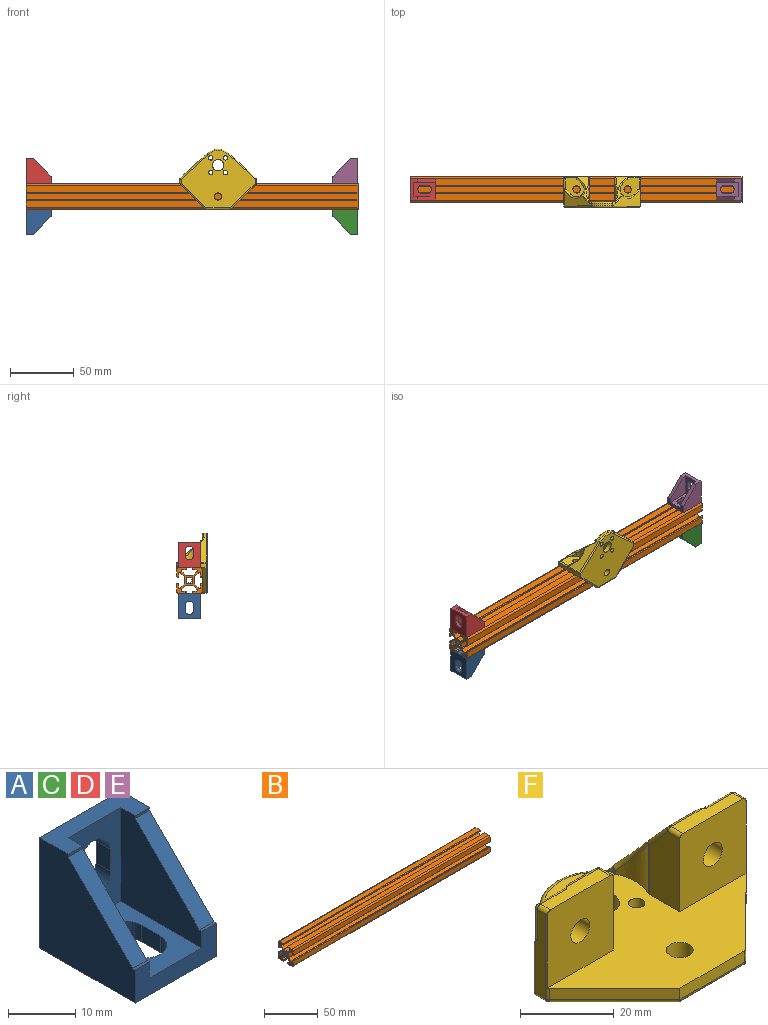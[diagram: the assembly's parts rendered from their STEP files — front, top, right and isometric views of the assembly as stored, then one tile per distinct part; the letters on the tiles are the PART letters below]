
ASSEMBLY  parts=6 mates=10
PART A: 24 faces, bbox 17x20x20 mm
  f0: plane 17x6mm, normal (0,0,1), area 69mm2, adj f3,f4,f5,f7,f8,f9,f12,f15
  f1: plane 17x11mm, normal (0,0,1), area 126.4mm2, adj f2,f7,f8,f9,f16,f17,f18,f19
  f2: plane 17x6mm, normal (0,-1,0), area 69mm2, adj f1,f3,f5,f6,f8,f9,f10,f14
  f3: plane 20x20mm, normal (1,0,0), area 295.1mm2, adj f0,f2,f4,f6,f13,f14,f15
  f4: plane 20x17mm, normal (0,1,0), area 279.4mm2, adj f0,f3,f5,f6,f20,f21,f22,f23
  f5: plane 20x20mm, normal (-1,0,0), area 295.1mm2, adj f0,f2,f4,f6,f10,f11,f12
  f6: plane 20x17mm, normal (0,0,-1), area 279.4mm2, adj f2,f3,f4,f5,f16,f17,f18,f19
  f7: plane 17x11mm, normal (0,-1,0), area 126.4mm2, adj f0,f1,f8,f9,f20,f21,f22,f23
  f8: plane 17x17mm, normal (-1,0,0), area 184.1mm2, adj f0,f1,f2,f7,f13,f14,f15
  f9: plane 17x17mm, normal (1,0,0), area 184.1mm2, adj f0,f1,f2,f7,f10,f11,f12
  f10: plane 3x0.5mm, normal (0,0,1), area 1.5mm2, adj f2,f5,f9,f11
  f11: plane 13.5x13.5mm, normal (0,-0.71,0.71), area 57.3mm2, adj f5,f9,f10,f12
  f12: plane 3x0.5mm, normal (0,-1,0), area 1.5mm2, adj f0,f5,f9,f11
  f13: plane 13.5x13.5mm, normal (0,-0.71,0.71), area 57.3mm2, adj f3,f8,f14,f15
  f14: plane 3x0.5mm, normal (0,0,1), area 1.5mm2, adj f2,f3,f8,f13
  f15: plane 3x0.5mm, normal (0,-1,0), area 1.5mm2, adj f0,f3,f8,f13
  f16: cylinder r=3.3mm len=6.6mm, axis (0,0,1), area 31.1mm2, adj f1,f6,f17,f19
  f17: plane 4x3mm, normal (1,0,0), area 12mm2, adj f1,f6,f16,f18
  f18: cylinder r=3.3mm len=6.6mm, axis (0,0,1), area 31.1mm2, adj f1,f6,f17,f19
  f19: plane 4x3mm, normal (-1,0,0), area 12mm2, adj f1,f6,f16,f18
  f20: cylinder r=3.3mm len=6.6mm, axis (0,-1,0), area 31.1mm2, adj f4,f7,f21,f23
  f21: plane 4x3mm, normal (-1,0,0), area 12mm2, adj f4,f7,f20,f22
  f22: cylinder r=3.3mm len=6.6mm, axis (0,-1,0), area 31.1mm2, adj f4,f7,f21,f23
  f23: plane 4x3mm, normal (1,0,0), area 12mm2, adj f4,f7,f20,f22
PART B: 106 faces, bbox 260x20x20 mm
  f0: cylinder r=2.11mm len=260mm, axis (1,0,0), area 428.9mm2, adj f1,f15,f16,f17
  f1: cylinder r=0.79mm len=260mm, axis (1,0,0), area 430.4mm2, adj f0,f2,f16,f17
  f2: plane 260x0.18mm, normal (0,-0.71,0.71), area 66mm2, adj f1,f3,f16,f17
  f3: cylinder r=0.79mm len=260mm, axis (1,0,0), area 430.4mm2, adj f2,f4,f16,f17
  f4: cylinder r=2.11mm len=260mm, axis (1,0,0), area 428.9mm2, adj f3,f5,f16,f17
  f5: cylinder r=0.79mm len=260mm, axis (1,0,0), area 430.4mm2, adj f4,f6,f16,f17
  f6: plane 260x0.18mm, normal (0,0.71,0.71), area 66mm2, adj f5,f7,f16,f17
  f7: cylinder r=0.79mm len=260mm, axis (1,0,0), area 430.4mm2, adj f6,f8,f16,f17
  f8: cylinder r=2.11mm len=260mm, axis (1,0,0), area 428.9mm2, adj f7,f9,f16,f17
  f9: cylinder r=0.79mm len=260mm, axis (1,0,0), area 430.4mm2, adj f8,f10,f16,f17
  f10: plane 260x0.18mm, normal (0,0.71,-0.71), area 66mm2, adj f9,f11,f16,f17
  f11: cylinder r=0.79mm len=260mm, axis (1,0,0), area 430.4mm2, adj f10,f12,f16,f17
  f12: cylinder r=2.11mm len=260mm, axis (1,0,0), area 428.9mm2, adj f11,f13,f16,f17
  f13: cylinder r=0.79mm len=260mm, axis (1,0,0), area 430.4mm2, adj f12,f14,f16,f17
  f14: plane 260x0.18mm, normal (0,-0.71,-0.71), area 66mm2, adj f13,f15,f16,f17
  f15: cylinder r=0.79mm len=260mm, axis (1,0,0), area 430.4mm2, adj f0,f14,f16,f17
  f16: plane 20x20mm, normal (-1,0,0), area 159.4mm2, adj f0,f1,f2,f3,f4,f5,f6,f7
  f17: plane 20x20mm, normal (1,0,0), area 159.4mm2, adj f0,f1,f2,f3,f4,f5,f6,f7
  f18: cylinder r=0.51mm len=260mm, axis (1,0,0), area 206.9mm2, adj f16,f17,f19,f105
  f19: plane 260x0.73mm, normal (0,1,0), area 188.7mm2, adj f16,f17,f18,f20
  f20: cylinder r=0.51mm len=260mm, axis (1,0,0), area 103.7mm2, adj f16,f17,f19,f21
  f21: plane 260x3.1mm, normal (0,0.71,-0.71), area 1141mm2, adj f16,f17,f20,f22
  f22: cylinder r=0.51mm len=260mm, axis (1,0,0), area 103.7mm2, adj f16,f17,f21,f23
  f23: plane 260x4.77mm, normal (0,0,-1), area 1239.6mm2, adj f16,f17,f22,f24
  f24: cylinder r=0.51mm len=260mm, axis (1,0,0), area 103.7mm2, adj f16,f17,f23,f25
  f25: plane 260x3.1mm, normal (0,-0.71,-0.71), area 1141mm2, adj f16,f17,f24,f26
  f26: cylinder r=0.51mm len=260mm, axis (1,0,0), area 103.7mm2, adj f16,f17,f25,f27
  f27: plane 260x0.73mm, normal (0,-1,0), area 188.7mm2, adj f16,f17,f26,f28
  f28: cylinder r=0.51mm len=260mm, axis (1,0,0), area 206.9mm2, adj f16,f17,f27,f29
  f29: plane 260x2.35mm, normal (0,0,1), area 610.7mm2, adj f16,f17,f28,f30
  f30: cylinder r=0.51mm len=260mm, axis (1,0,0), area 206.9mm2, adj f16,f17,f29,f31
  f31: plane 260x0.48mm, normal (0,-1,0), area 125.8mm2, adj f16,f17,f30,f32
  f32: cylinder r=0.51mm len=260mm, axis (1,0,0), area 206.9mm2, adj f16,f17,f31,f33
  f33: plane 260x5.36mm, normal (0,0,-1), area 1394.1mm2, adj f16,f17,f32,f34
  f34: cylinder r=1.51mm len=260mm, axis (1,0,0), area 611mm2, adj f16,f17,f33,f35
  f35: plane 260x5.36mm, normal (0,1,0), area 1394.1mm2, adj f16,f17,f34,f36
  f36: cylinder r=0.51mm len=260mm, axis (1,0,0), area 206.9mm2, adj f16,f17,f35,f37
  f37: plane 260x0.48mm, normal (0,0,1), area 125.8mm2, adj f16,f17,f36,f38
  f38: cylinder r=0.51mm len=260mm, axis (1,0,0), area 206.9mm2, adj f16,f17,f37,f39
  f39: plane 260x2.35mm, normal (0,-1,0), area 610.7mm2, adj f16,f17,f38,f40
  f40: cylinder r=0.51mm len=260mm, axis (1,0,0), area 206.9mm2, adj f16,f17,f39,f41
  f41: plane 260x0.73mm, normal (0,0,1), area 188.7mm2, adj f16,f17,f40,f42
  f42: cylinder r=0.51mm len=260mm, axis (1,0,0), area 103.7mm2, adj f16,f17,f41,f43
  f43: plane 260x3.1mm, normal (0,0.71,0.71), area 1141mm2, adj f16,f17,f42,f44
  f44: cylinder r=0.51mm len=260mm, axis (1,0,0), area 103.7mm2, adj f16,f17,f43,f45
  f45: plane 260x4.77mm, normal (0,1,0), area 1239.6mm2, adj f16,f17,f44,f46
  f46: cylinder r=0.51mm len=260mm, axis (1,0,0), area 103.7mm2, adj f16,f17,f45,f47
  f47: plane 260x3.1mm, normal (0,0.71,-0.71), area 1141mm2, adj f16,f17,f46,f48
  f48: cylinder r=0.51mm len=260mm, axis (1,0,0), area 103.7mm2, adj f16,f17,f47,f49
  f49: plane 260x0.73mm, normal (0,0,-1), area 188.7mm2, adj f16,f17,f48,f50
  f50: cylinder r=0.51mm len=260mm, axis (1,0,0), area 206.9mm2, adj f16,f17,f49,f51
  f51: plane 260x2.35mm, normal (0,-1,0), area 610.7mm2, adj f16,f17,f50,f52
  f52: cylinder r=0.51mm len=260mm, axis (1,0,0), area 206.9mm2, adj f16,f17,f51,f53
  f53: plane 260x0.48mm, normal (0,0,-1), area 125.8mm2, adj f16,f17,f52,f54
  f54: cylinder r=0.51mm len=260mm, axis (1,0,0), area 206.9mm2, adj f16,f17,f53,f55
  f55: plane 260x5.36mm, normal (0,1,0), area 1394.1mm2, adj f16,f17,f54,f56
  f56: cylinder r=1.51mm len=260mm, axis (1,0,0), area 611mm2, adj f16,f17,f55,f57
  f57: plane 260x5.36mm, normal (0,0,1), area 1394.1mm2, adj f16,f17,f56,f58
  f58: cylinder r=0.51mm len=260mm, axis (1,0,0), area 206.9mm2, adj f16,f17,f57,f59
  f59: plane 260x0.48mm, normal (0,-1,0), area 125.8mm2, adj f16,f17,f58,f60
  f60: cylinder r=0.51mm len=260mm, axis (1,0,0), area 206.9mm2, adj f16,f17,f59,f61
  f61: plane 260x2.35mm, normal (0,0,-1), area 610.7mm2, adj f16,f17,f60,f62
  f62: cylinder r=0.51mm len=260mm, axis (1,0,0), area 206.9mm2, adj f16,f17,f61,f63
  f63: plane 260x0.73mm, normal (0,-1,0), area 188.7mm2, adj f16,f17,f62,f64
  f64: cylinder r=0.51mm len=260mm, axis (1,0,0), area 103.7mm2, adj f16,f17,f63,f65
  f65: plane 260x3.1mm, normal (0,-0.71,0.71), area 1141mm2, adj f16,f17,f64,f66
  f66: cylinder r=0.51mm len=260mm, axis (1,0,0), area 103.7mm2, adj f16,f17,f65,f67
  f67: plane 260x4.77mm, normal (0,0,1), area 1239.6mm2, adj f16,f17,f66,f68
  f68: cylinder r=0.51mm len=260mm, axis (1,0,0), area 103.7mm2, adj f16,f17,f67,f69
  f69: plane 260x3.1mm, normal (0,0.71,0.71), area 1141mm2, adj f16,f17,f68,f70
  f70: cylinder r=0.51mm len=260mm, axis (1,0,0), area 103.7mm2, adj f16,f17,f69,f71
  f71: plane 260x0.73mm, normal (0,1,0), area 188.7mm2, adj f16,f17,f70,f72
  f72: cylinder r=0.51mm len=260mm, axis (1,0,0), area 206.9mm2, adj f16,f17,f71,f73
  f73: plane 260x2.35mm, normal (0,0,-1), area 610.7mm2, adj f16,f17,f72,f74
  f74: cylinder r=0.51mm len=260mm, axis (1,0,0), area 206.9mm2, adj f16,f17,f73,f75
  f75: plane 260x0.48mm, normal (0,1,0), area 125.8mm2, adj f16,f17,f74,f76
  f76: cylinder r=0.51mm len=260mm, axis (1,0,0), area 206.9mm2, adj f16,f17,f75,f77
  f77: plane 260x5.36mm, normal (0,0,1), area 1394.1mm2, adj f16,f17,f76,f78
  f78: cylinder r=1.51mm len=260mm, axis (1,0,0), area 611mm2, adj f16,f17,f77,f79
  f79: plane 260x5.36mm, normal (0,-1,0), area 1394.1mm2, adj f16,f17,f78,f80
  f80: cylinder r=0.51mm len=260mm, axis (1,0,0), area 206.9mm2, adj f16,f17,f79,f81
  f81: plane 260x0.48mm, normal (0,0,-1), area 125.8mm2, adj f16,f17,f80,f82
  f82: cylinder r=0.51mm len=260mm, axis (1,0,0), area 206.9mm2, adj f16,f17,f81,f83
  f83: plane 260x2.35mm, normal (0,1,0), area 610.7mm2, adj f16,f17,f82,f84
  f84: cylinder r=0.51mm len=260mm, axis (1,0,0), area 206.9mm2, adj f16,f17,f83,f85
  f85: plane 260x0.73mm, normal (0,0,-1), area 188.7mm2, adj f16,f17,f84,f86
  f86: cylinder r=0.51mm len=260mm, axis (1,0,0), area 103.7mm2, adj f16,f17,f85,f87
  f87: plane 260x3.1mm, normal (0,-0.71,-0.71), area 1141mm2, adj f16,f17,f86,f88
  f88: cylinder r=0.51mm len=260mm, axis (1,0,0), area 103.7mm2, adj f16,f17,f87,f89
  f89: plane 260x4.77mm, normal (0,-1,0), area 1239.6mm2, adj f16,f17,f88,f90
  f90: cylinder r=0.51mm len=260mm, axis (1,0,0), area 103.7mm2, adj f16,f17,f89,f91
  f91: plane 260x3.1mm, normal (0,-0.71,0.71), area 1141mm2, adj f16,f17,f90,f92
  f92: cylinder r=0.51mm len=260mm, axis (1,0,0), area 103.7mm2, adj f16,f17,f91,f93
  f93: plane 260x0.73mm, normal (0,0,1), area 188.7mm2, adj f16,f17,f92,f94
  f94: cylinder r=0.51mm len=260mm, axis (1,0,0), area 206.9mm2, adj f16,f17,f93,f95
  f95: plane 260x2.35mm, normal (0,1,0), area 610.7mm2, adj f16,f17,f94,f96
  f96: cylinder r=0.51mm len=260mm, axis (1,0,0), area 206.9mm2, adj f16,f17,f95,f97
  f97: plane 260x0.48mm, normal (0,0,1), area 125.8mm2, adj f16,f17,f96,f98
  f98: cylinder r=0.51mm len=260mm, axis (1,0,0), area 206.9mm2, adj f16,f17,f97,f99
  f99: plane 260x5.36mm, normal (0,-1,0), area 1394.1mm2, adj f16,f17,f98,f100
  f100: cylinder r=1.51mm len=260mm, axis (1,0,0), area 611mm2, adj f16,f17,f99,f101
  f101: plane 260x5.36mm, normal (0,0,-1), area 1394.1mm2, adj f16,f17,f100,f102
  f102: cylinder r=0.51mm len=260mm, axis (1,0,0), area 206.9mm2, adj f16,f17,f101,f103
  f103: plane 260x0.48mm, normal (0,1,0), area 125.8mm2, adj f16,f17,f102,f104
  f104: cylinder r=0.51mm len=260mm, axis (1,0,0), area 206.9mm2, adj f16,f17,f103,f105
  f105: plane 260x2.35mm, normal (0,0,1), area 610.7mm2, adj f16,f17,f18,f104
PART C: same geometry as A
PART D: same geometry as A
PART E: same geometry as A
PART F: 95 faces, bbox 62x48.1x25 mm
  f0: plane 19x9.11mm, normal (1,0,0), area 155.9mm2, adj f7,f9,f53,f54,f55
  f1: plane 0.85x0.76mm, normal (1,0,0), area 0.3mm2, adj f7,f56,f77
  f2: plane 19x9.11mm, normal (-1,0,0), area 155.9mm2, adj f7,f12,f49,f50,f51
  f3: plane 0.85x0.76mm, normal (-1,0,0), area 0.3mm2, adj f7,f52,f78
  f4: plane 19.71x19.71mm, normal (-0.71,-0.71,0), area 83.6mm2, adj f5,f7,f62,f63
  f5: plane 19.59x3mm, normal (0,-1,0), area 58.8mm2, adj f4,f7,f57,f60
  f6: plane 19.71x19.71mm, normal (0.71,-0.71,0), area 83.6mm2, adj f7,f13,f57,f61
  f7: plane 59.91x46mm, normal (0,0,1), area 1177mm2, adj f0,f1,f2,f3,f4,f5,f6,f9
  f8: plane 58x45mm, normal (0,0,-1), area 1550.2mm2, adj f18,f23,f34,f35,f36,f37,f60,f61
  f9: plane 20x19.91mm, normal (0,-1,0), area 372.3mm2, adj f0,f7,f11,f21,f53,f59,f62
  f10: plane 22.01x3.15mm, normal (-1,0,0), area 64.7mm2, adj f44,f59,f62,f67,f73,f89
  f11: plane 18.01x3.56mm, normal (0,0,1), area 59.5mm2, adj f9,f42,f53,f59,f71,f87
  f12: plane 20x20mm, normal (0,-1,0), area 374.1mm2, adj f2,f7,f13,f14,f22,f49,f70
  f13: plane 22.01x3.57mm, normal (1,0,0), area 73.8mm2, adj f6,f12,f40,f64,f70,f84,f94
  f14: plane 18.01x3.56mm, normal (0,0,1), area 59.5mm2, adj f12,f38,f49,f70,f82,f92
  f15: plane 21.24x19.43mm, normal (0.67,0.74,0), area 187.8mm2, adj f16,f40,f41,f48,f66,f78,f85,f94
  f16: cylinder r=12.5mm len=16.87mm, axis (0,0,-1), area 37mm2, adj f15,f17,f47,f68
  f17: plane 21.24x19.43mm, normal (-0.67,0.74,0), area 187.8mm2, adj f16,f44,f45,f46,f69,f77,f89,f90
  f18: cylinder r=4.5mm len=9mm, axis (0,0,-1), area 113.1mm2, adj f7,f8
  f19: plane 18.3x16.47mm, normal (0,0.74,0.67), area 68.3mm2, adj f38,f39,f50,f78,f80,f85,f92
  f20: plane 18.3x16.47mm, normal (0,0.74,0.67), area 68.3mm2, adj f42,f43,f54,f75,f77,f87,f90
  f21: cylinder r=2.85mm len=5.7mm, axis (0,-1,0), area 71.6mm2, adj f9,f31
  f22: cylinder r=2.85mm len=5.7mm, axis (0,-1,0), area 71.6mm2, adj f12,f27
  f23: cylinder r=2.85mm len=5.7mm, axis (0,0,-1), area 71.6mm2, adj f7,f8
  f24: plane 3.6x3.6mm, normal (-0.71,0,0.71), area 8.4mm2, adj f25,f27,f40
  f25: cylinder r=5.95mm len=12.18mm, axis (0,-1,0), area 144.3mm2, adj f24,f26,f27,f39,f41
  f26: plane 3.59x3.59mm, normal (0.71,0,-0.71), area 8.2mm2, adj f25,f27,f38
  f27: plane 15.06x15.06mm, normal (0,1,0), area 146.5mm2, adj f22,f24,f25,f26,f38,f40,f82,f84
  f28: plane 3.59x3.59mm, normal (-0.71,0,-0.71), area 8.2mm2, adj f29,f31,f42
  f29: cylinder r=5.95mm len=12.18mm, axis (0,-1,0), area 144.3mm2, adj f28,f30,f31,f43,f45
  f30: plane 3.6x3.6mm, normal (0.71,0,0.71), area 8.4mm2, adj f29,f31,f44
  f31: plane 15.06x15.06mm, normal (0,1,0), area 146.5mm2, adj f21,f28,f29,f30,f42,f44,f71,f73
  f32: cylinder r=11.25mm len=12.83mm, axis (0,0,-1), area 70.1mm2, adj f7,f55,f56,f75
  f33: cylinder r=11.25mm len=12.83mm, axis (0,0,-1), area 70.1mm2, adj f7,f51,f52,f80
  f34: cylinder r=1.75mm len=4mm, axis (0,0,-1), area 44mm2, adj f7,f8
  f35: cylinder r=1.75mm len=4mm, axis (0,0,-1), area 44mm2, adj f7,f8
  f36: cylinder r=1.75mm len=4mm, axis (0,0,-1), area 44mm2, adj f7,f8
  f37: cylinder r=1.75mm len=4mm, axis (0,0,-1), area 44mm2, adj f7,f8
  f38: cylinder r=1mm len=6.72mm, axis (0.6,-0.54,0.6), area 14.9mm2, adj f14,f19,f26,f27,f39,f82,f92
  f39: bspline ~11.4x11mm, area 21.2mm2, adj f19,f25,f38,f41,f85
  f40: cylinder r=1mm len=6.71mm, axis (0.59,-0.54,0.59), area 15mm2, adj f13,f15,f24,f27,f41,f84,f94
  f41: bspline ~11.4x11.16mm, area 21mm2, adj f15,f25,f39,f40,f85
  f42: cylinder r=1mm len=6.72mm, axis (0.6,0.54,-0.6), area 14.9mm2, adj f11,f20,f28,f31,f43,f71,f87
  f43: bspline ~10.16x9.88mm, area 21.2mm2, adj f20,f29,f42,f45,f90
  f44: cylinder r=1mm len=6.71mm, axis (0.59,0.54,-0.59), area 15mm2, adj f10,f17,f30,f31,f45,f73,f89
  f45: bspline ~11.4x11.16mm, area 21mm2, adj f17,f29,f43,f44,f90
  f46: cylinder r=1mm len=2.93mm, axis (0.74,0.67,0), area 4.2mm2, adj f7,f17,f47,f77
  f47: torus R=11.5mm, axis (0,0,1), area 28.2mm2, adj f7,f16,f46,f48
  f48: cylinder r=1mm len=2.93mm, axis (0.74,-0.67,0), area 4.2mm2, adj f7,f15,f47,f78
  f49: cylinder r=1mm len=3.55mm, axis (0,1,0), area 5.6mm2, adj f2,f12,f14,f91
  f50: cylinder r=1mm len=6.84mm, axis (0,-0.67,0.74), area 13mm2, adj f2,f19,f81,f91
  f51: cylinder r=1mm len=12.83mm, axis (0,0,-1), area 5.8mm2, adj f2,f7,f33,f81
  f52: cylinder r=1mm len=0.85mm, axis (0,0,-1), area 0.4mm2, adj f3,f7,f33,f79
  f53: cylinder r=1mm len=3.55mm, axis (0,-1,0), area 5.6mm2, adj f0,f9,f11,f86
  f54: cylinder r=1mm len=6.84mm, axis (0,-0.67,0.74), area 13mm2, adj f0,f20,f74,f86
  f55: cylinder r=1mm len=12.83mm, axis (0,0,-1), area 5.8mm2, adj f0,f7,f32,f74
  f56: cylinder r=1mm len=0.85mm, axis (0,0,-1), area 0.4mm2, adj f1,f7,f32,f76
  f57: cylinder r=1mm len=3mm, axis (0,0,-1), area 2.4mm2, adj f5,f6,f7,f58
  f58: sphere r=1mm, area 0.8mm2, adj f57,f60,f61
  f59: cylinder r=1mm len=3mm, axis (0,1,0), area 4.6mm2, adj f9,f10,f11,f62,f72
  f60: cylinder r=1mm len=19.59mm, axis (1,0,0), area 30.4mm2, adj f5,f8,f58,f63
  f61: cylinder r=1mm len=20.41mm, axis (0.71,0.71,0), area 43.5mm2, adj f6,f8,f58,f64
  f62: cylinder r=1mm len=22.41mm, axis (0,0,-1), area 10.6mm2, adj f4,f7,f9,f10,f59,f65
  f63: cylinder r=1mm len=20.41mm, axis (0.71,-0.71,0), area 43.5mm2, adj f4,f8,f60,f65
  f64: cylinder r=1mm len=3.56mm, axis (0,1,0), area 5.3mm2, adj f8,f13,f61,f93
  f65: sphere r=1mm, area 0.8mm2, adj f62,f63,f67
  f66: cylinder r=1mm len=21.91mm, axis (-0.74,0.67,0), area 45.2mm2, adj f8,f15,f68,f93
  f67: cylinder r=1mm len=3.15mm, axis (0,-1,0), area 4.9mm2, adj f8,f10,f65,f88
  f68: torus R=11.5mm, axis (0,0,1), area 28.2mm2, adj f8,f16,f66,f69
  f69: cylinder r=1mm len=21.91mm, axis (-0.74,-0.67,0), area 45.2mm2, adj f8,f17,f68,f88
  f70: cylinder r=1mm len=3mm, axis (0,-1,0), area 4.7mm2, adj f12,f13,f14,f83
  f71: cylinder r=1mm len=8.87mm, axis (-1,0,0), area 13.1mm2, adj f11,f31,f42,f72
  f72: sphere r=1mm, area 1.6mm2, adj f59,f71,f73
  f73: cylinder r=1mm len=8.87mm, axis (0,0,-1), area 13.1mm2, adj f10,f31,f44,f72
  f74: sphere r=1mm, area 0.2mm2, adj f54,f55,f75
  f75: bspline ~12.65x11.09mm, area 25.1mm2, adj f20,f32,f74,f76
  f76: sphere r=1mm, area 0.4mm2, adj f56,f75,f77
  f77: cylinder r=1mm len=2.83mm, axis (0,-0.67,0.74), area 2.4mm2, adj f1,f7,f17,f20,f46,f76,f90
  f78: cylinder r=1mm len=2.83mm, axis (0,-0.67,0.74), area 2.4mm2, adj f3,f7,f15,f19,f48,f79,f85
  f79: sphere r=1mm, area 0.4mm2, adj f52,f78,f80
  f80: bspline ~12.65x11.09mm, area 25.1mm2, adj f19,f33,f79,f81
  f81: sphere r=1mm, area 0.2mm2, adj f50,f51,f80
  f82: cylinder r=1mm len=8.87mm, axis (-1,0,0), area 13.1mm2, adj f14,f27,f38,f83
  f83: sphere r=1mm, area 2.1mm2, adj f70,f82,f84
  f84: cylinder r=1mm len=8.87mm, axis (0,0,1), area 13.1mm2, adj f13,f27,f40,f83
  f85: cylinder r=1mm len=6.69mm, axis (-0.59,0.54,-0.6), area 8.5mm2, adj f15,f19,f39,f41,f78
  f86: sphere r=1mm, area 0.8mm2, adj f53,f54,f87
  f87: cylinder r=1mm len=9.65mm, axis (1,0,0), area 7.5mm2, adj f11,f20,f42,f86
  f88: sphere r=1mm, area 0.8mm2, adj f67,f69,f89
  f89: cylinder r=1mm len=13.63mm, axis (0,0,1), area 10.7mm2, adj f10,f17,f44,f88
  f90: cylinder r=1mm len=6.69mm, axis (0.59,0.54,-0.6), area 8.5mm2, adj f17,f20,f43,f45,f77
  f91: sphere r=1mm, area 1.2mm2, adj f49,f50,f92
  f92: cylinder r=1mm len=9.65mm, axis (1,0,0), area 7.5mm2, adj f14,f19,f38,f91
  f93: sphere r=1mm, area 0.5mm2, adj f64,f66,f94
  f94: cylinder r=1mm len=13.63mm, axis (0,0,1), area 10.7mm2, adj f13,f15,f40,f93
PLACE A rot(axis=(0.71,-0.71,0),180deg) t=(-535.36,-98.27,-111.42)mm
PLACE B rot(axis=(0,-1,0),180deg) t=(-449.4,-98.27,71.88)mm
PLACE C rot(axis=(0.71,0.71,0),180deg) t=(-295.36,-98.27,-111.42)mm
PLACE D rot(axis=(0,0,1),90deg) t=(-535.36,-98.27,-91.42)mm
PLACE E rot(axis=(0,0,-1),90deg) t=(-295.36,-98.28,-91.42)mm
PLACE F rot(axis=(0,-0.71,-0.71),180deg) t=(-198.31,-112.27,-14.74)mm
MATE planar A.f4 <-> B.f12  axis (-1,0,0) through (-545.36,-98.27,-121.09)mm
MATE planar E.f4 <-> B.f0  axis (1,0,0) through (-285.36,-98.28,-81.75)mm
MATE planar D.f4 <-> B.f17  axis (-1,0,0) through (-545.36,-98.27,-81.75)mm
MATE planar C.f4 <-> B.f16  axis (1,0,0) through (-285.36,-98.27,-121.09)mm
MATE planar D.f16 <-> B.f33  axis (0,0,-1) through (-535.86,-98.27,-91.42)mm
MATE planar E.f6 <-> B.f101  axis (0,0,-1) through (-295.03,-98.28,-91.42)mm
MATE planar F.f22 <-> B.f33  axis (0,0,-1) through (-414.92,-98.27,-91.42)mm
MATE planar B.f99 <-> F.f7  axis (0,-1,0) through (-415.36,-108.27,-95.6)mm
MATE planar C.f6 <-> B.f57  axis (0,0,1) through (-295.03,-98.27,-111.42)mm
MATE planar A.f6 <-> B.f77  axis (0,0,1) through (-535.86,-94.97,-111.42)mm
